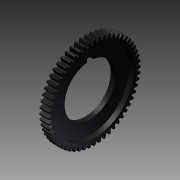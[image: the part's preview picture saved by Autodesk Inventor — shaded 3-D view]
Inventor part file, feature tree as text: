
AUTODESK INVENTOR PART (.ipt)
format: ipt  version: 2012 (Build 160160000, 160)  size: 1,009,152 bytes
history: native  units: in
note: dims shown in document units (in); Inventor stores cm internally (conversion verified against a paired STEP export)
features: sketch x2, extrude x1, imported_body x1
ambient origin geometry x8: Origin, YZ Plane, XZ Plane, XY Plane, X Axis, Y Axis, Z Axis, Center Point
feature tree (4):
  sketch  "Sketch1"  dims[d0=1.0in d1=0.0in d2=0.0in]
  extrude  "Extrusion1"  TaperAngle=0.0deg  [1 undecoded]
  imported_body  "Base1"
  sketch  "Sketch2"  dims[d3=0.125in d4=0.125in d5=0.0625in d6=0.4375in]
note: 1 required parameter value undecoded (feature->parameter linkage not recoverable at this tier; creation-order binding heuristic only, values carry confidence <= 0.55)
